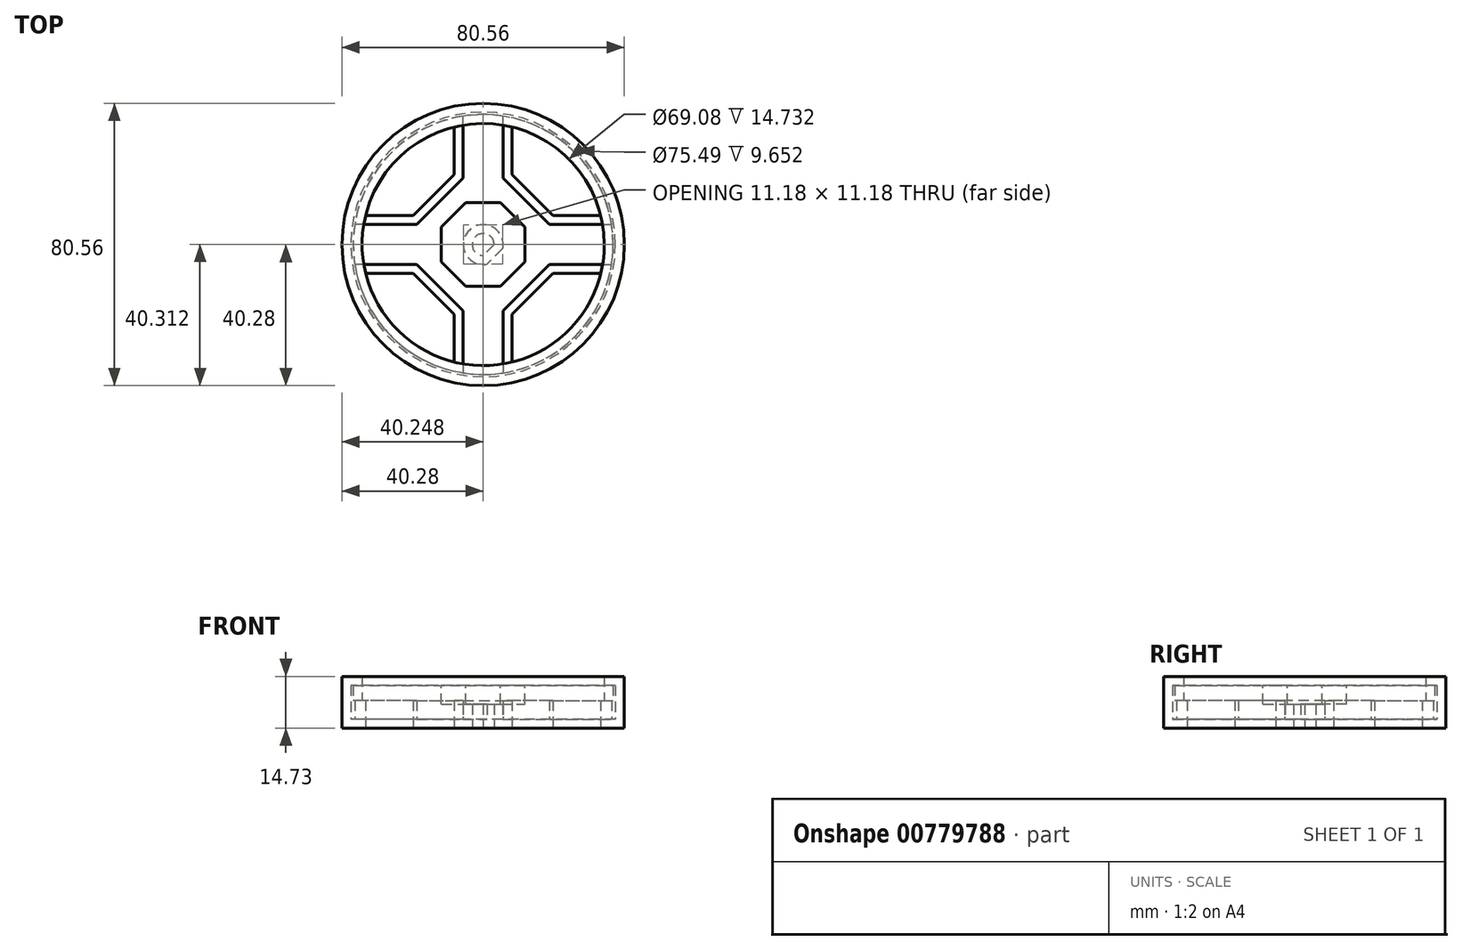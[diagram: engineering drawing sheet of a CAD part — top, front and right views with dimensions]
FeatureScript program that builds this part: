
annotation { "Feature Type Name" : "Feature", "Feature Type Description" : "" }
export const myFeature = defineFeature(function(context is Context, id is Id, definition is map)
    precondition{}
    {
        {
            var Q0;
            Q0=qCreatedBy(makeId("Top.planeOp"),FACE);
            var sketch = newSketch(context, id + "F0", { "sketchPlane" : qUnion([Q0])});
            skCircle(sketch, "E0", {"center": v(0, 0) * mm, "radius": 43.73 * mm});
            skCircle(sketch, "E1", {"center": v(0, 0) * mm, "radius": 34.6 * mm});
            skCircle(sketch, "E2.cCircle", {"center": v(0, 0) * mm, "radius": 19.97 * mm, "construction": true});
            skLineSegment(sketch, "E2.0", {"start": v(-8.27, 19.97) * mm, "end": v(8.27, 19.97) * mm});
            skLineSegment(sketch, "E2.1", {"start": v(8.27, 19.97) * mm, "end": v(19.97, 8.27) * mm});
            skLineSegment(sketch, "E2.2", {"start": v(19.97, 8.27) * mm, "end": v(19.97, -8.27) * mm});
            skLineSegment(sketch, "E2.3", {"start": v(19.97, -8.27) * mm, "end": v(8.27, -19.97) * mm});
            skLineSegment(sketch, "E2.4", {"start": v(8.27, -19.97) * mm, "end": v(-8.27, -19.97) * mm});
            skLineSegment(sketch, "E2.5", {"start": v(-8.27, -19.97) * mm, "end": v(-19.97, -8.27) * mm});
            skLineSegment(sketch, "E2.6", {"start": v(-19.97, -8.27) * mm, "end": v(-19.97, 8.27) * mm});
            skLineSegment(sketch, "E2.7", {"start": v(-19.97, 8.27) * mm, "end": v(-8.27, 19.97) * mm});
            skPoint(sketch, "E2.0.midPoint", {"position": v(0, 19.97) * mm});
            skLineSegment(sketch, "E3", {"start": v(8.27, -19.97) * mm, "end": v(8.27, -33.59) * mm});
            skLineSegment(sketch, "E4", {"start": v(8.27, -33.59) * mm, "end": v(8.27, -19.97) * mm});
            skLineSegment(sketch, "E5", {"start": v(-8.27, -19.97) * mm, "end": v(-8.27, -33.59) * mm});
            skLineSegment(sketch, "E6", {"start": v(-8.27, -33.59) * mm, "end": v(-8.27, -19.97) * mm});
            skLineSegment(sketch, "E7", {"start": v(-19.97, -8.27) * mm, "end": v(-33.59, -8.27) * mm});
            skLineSegment(sketch, "E8", {"start": v(-33.59, -8.27) * mm, "end": v(-19.97, -8.27) * mm});
            skLineSegment(sketch, "E9", {"start": v(-19.97, 8.27) * mm, "end": v(-33.59, 8.27) * mm});
            skLineSegment(sketch, "E10", {"start": v(-33.59, 8.27) * mm, "end": v(-19.97, 8.27) * mm});
            skLineSegment(sketch, "E11", {"start": v(-8.27, 19.97) * mm, "end": v(-8.27, 33.59) * mm});
            skLineSegment(sketch, "E12", {"start": v(-8.27, 33.59) * mm, "end": v(-8.27, 19.97) * mm});
            skLineSegment(sketch, "E13", {"start": v(8.27, 19.97) * mm, "end": v(8.27, 33.59) * mm});
            skLineSegment(sketch, "E14", {"start": v(8.27, 33.59) * mm, "end": v(8.27, 19.97) * mm});
            skLineSegment(sketch, "E15", {"start": v(19.97, 8.27) * mm, "end": v(33.59, 8.27) * mm});
            skLineSegment(sketch, "E16", {"start": v(33.59, 8.27) * mm, "end": v(19.97, 8.27) * mm});
            skLineSegment(sketch, "E17", {"start": v(19.97, -8.27) * mm, "end": v(33.59, -8.27) * mm});
            skLineSegment(sketch, "E18", {"start": v(33.59, -8.27) * mm, "end": v(19.97, -8.27) * mm});
            skSolve(sketch);
        }
        {
            var Q0;
            Q0=makeQuery(id+"F0.imprint","IMPRINT",FACE,{"disambiguationData":[TD([[makeQuery(id+"F0.imprint","IMPRINT",EDGE,{"derivedFrom":sQuery(id+"F0.wireOp",EDGE,"E2.0")}),-1.0]])]});
            var Q1;
            Q1=makeQuery(id+"F0.imprint","IMPRINT",FACE,{"disambiguationData":[TD([[makeQuery(id+"F0.imprint","IMPRINT",EDGE,{"derivedFrom":sQuery(id+"F0.wireOp",EDGE,"E2.6")}),1.0]])]});
            var Q2;
            Q2=makeQuery(id+"F0.imprint","IMPRINT",FACE,{"disambiguationData":[TD([[makeQuery(id+"F0.imprint","IMPRINT",EDGE,{"derivedFrom":sQuery(id+"F0.wireOp",EDGE,"E2.0")}),1.0]])]});
            var Q3;
            Q3=makeQuery(id+"F0.imprint","IMPRINT",FACE,{"disambiguationData":[TD([[makeQuery(id+"F0.imprint","IMPRINT",EDGE,{"derivedFrom":sQuery(id+"F0.wireOp",EDGE,"E2.4")}),1.0]])]});
            var Q4;
            Q4=makeQuery(id+"F0.imprint","IMPRINT",FACE,{"disambiguationData":[TD([[makeQuery(id+"F0.imprint","IMPRINT",EDGE,{"derivedFrom":sQuery(id+"F0.wireOp",EDGE,"E2.2")}),1.0]])]});
            extrude(context, id + "F1", {"entities" : qUnion([Q0, Q1, Q2, Q3, Q4]), "depth" : 7.87 * mm, "offsetDistance" : 25.4 * mm});
        }
        {
            var Q0;
            Q0=qCreatedBy(makeId("Top.planeOp"),FACE);
            var sketch = newSketch(context, id + "F2", { "sketchPlane" : qUnion([Q0])});
            skCircle(sketch, "E19", {"center": v(0, 0) * mm, "radius": 34.54 * mm});
            skCircle(sketch, "E20", {"center": v(0, 0) * mm, "radius": 40.28 * mm});
            skSolve(sketch);
        }
        {
            var Q0;
            Q0 = qSketchRegion(id + "F2", true);
            extrude(context, id + "F3", {"entities" : qUnion([Q0]), "operationType" : NewBodyOperationType.ADD, "depth" : 14.73 * mm, "offsetDistance" : 25.4 * mm});
        }
        {
            var Q0;
            Q0=makeQuery(id+"F3.boolean.opBoolean","MERGE",FACE,{"derivedFrom":[makeQuery(id+"F1.opExtrude","CAP_FACE",FACE,{"disambiguationData":[OSD([sQuery(id+"F0.wireOp",EDGE,"E1"),sQuery(id+"F0.wireOp",EDGE,"E2.1"),sQuery(id+"F0.wireOp",EDGE,"E2.3"),sQuery(id+"F0.wireOp",EDGE,"E2.5"),sQuery(id+"F0.wireOp",EDGE,"E2.7"),sQuery(id+"F0.wireOp",EDGE,"E4"),sQuery(id+"F0.wireOp",EDGE,"E6"),sQuery(id+"F0.wireOp",EDGE,"E8"),sQuery(id+"F0.wireOp",EDGE,"E10"),sQuery(id+"F0.wireOp",EDGE,"E12"),sQuery(id+"F0.wireOp",EDGE,"E14"),sQuery(id+"F0.wireOp",EDGE,"E16"),sQuery(id+"F0.wireOp",EDGE,"E18")])],"isStart":true}),makeQuery(id+"F3.opExtrude","CAP_FACE",FACE,{"disambiguationData":[OSD([sQuery(id+"F2.wireOp",EDGE,"E19"),sQuery(id+"F2.wireOp",EDGE,"E20")])],"isStart":true})]});
            var sketch = newSketch(context, id + "F4", { "sketchPlane" : qUnion([Q0])});
            skArc(sketch, "E21", {"start": v(0, 3.14) * mm, "mid": v(-2.22, -2.22) * mm, "end": v(3.14, 0) * mm});
            skLineSegment(sketch, "E22", {"start": v(3.14, 0) * mm, "end": v(0, 3.14) * mm});
            skSolve(sketch);
        }
        {
            var Q0;
            Q0 = qSketchRegion(id + "F4", true);
            extrude(context, id + "F5", {"entities" : qUnion([Q0]), "operationType" : NewBodyOperationType.REMOVE, "oppositeDirection" : true, "depth" : 25.4 * mm, "offsetDistance" : 25.4 * mm});
        }
        {
            var Q0;
            Q0=makeQuery(id+"F1.opExtrude","CAP_FACE",FACE,{"disambiguationData":[OSD([sQuery(id+"F0.wireOp",EDGE,"E1"),sQuery(id+"F0.wireOp",EDGE,"E2.1"),sQuery(id+"F0.wireOp",EDGE,"E2.3"),sQuery(id+"F0.wireOp",EDGE,"E2.5"),sQuery(id+"F0.wireOp",EDGE,"E2.7"),sQuery(id+"F0.wireOp",EDGE,"E4"),sQuery(id+"F0.wireOp",EDGE,"E6"),sQuery(id+"F0.wireOp",EDGE,"E8"),sQuery(id+"F0.wireOp",EDGE,"E10"),sQuery(id+"F0.wireOp",EDGE,"E12"),sQuery(id+"F0.wireOp",EDGE,"E14"),sQuery(id+"F0.wireOp",EDGE,"E16"),sQuery(id+"F0.wireOp",EDGE,"E18")])],"isStart":false});
            shell(context, id + "F6", {"entities" : qUnion([Q0]), "thickness" : 2.54 * mm});
        }
        {
            var Q0;
            Q0=makeQuery(id+"F6.opShell","OFFSET_FACE",FACE,{"disambiguationData":[OSD([sQuery(id+"F0.wireOp",EDGE,"E1"),sQuery(id+"F0.wireOp",EDGE,"E2.1"),sQuery(id+"F0.wireOp",EDGE,"E2.3"),sQuery(id+"F0.wireOp",EDGE,"E2.5"),sQuery(id+"F0.wireOp",EDGE,"E2.7"),sQuery(id+"F0.wireOp",EDGE,"E4"),sQuery(id+"F0.wireOp",EDGE,"E6"),sQuery(id+"F0.wireOp",EDGE,"E8"),sQuery(id+"F0.wireOp",EDGE,"E10"),sQuery(id+"F0.wireOp",EDGE,"E12"),sQuery(id+"F0.wireOp",EDGE,"E14"),sQuery(id+"F0.wireOp",EDGE,"E16"),sQuery(id+"F0.wireOp",EDGE,"E18"),sQuery(id+"F2.wireOp",EDGE,"E19"),sQuery(id+"F2.wireOp",EDGE,"E20")])]});
            var sketch = newSketch(context, id + "F7", { "sketchPlane" : qUnion([Q0])});
            skCircle(sketch, "E23.cCircle", {"center": v(0, 0) * mm, "radius": 11.92 * mm, "construction": true});
            skLineSegment(sketch, "E23.0", {"start": v(11.92, 4.94) * mm, "end": v(11.92, -4.94) * mm});
            skLineSegment(sketch, "E23.1", {"start": v(11.92, -4.94) * mm, "end": v(4.94, -11.92) * mm});
            skLineSegment(sketch, "E23.2", {"start": v(4.94, -11.92) * mm, "end": v(-4.94, -11.92) * mm});
            skLineSegment(sketch, "E23.3", {"start": v(-4.94, -11.92) * mm, "end": v(-11.92, -4.94) * mm});
            skLineSegment(sketch, "E23.4", {"start": v(-11.92, -4.94) * mm, "end": v(-11.92, 4.94) * mm});
            skLineSegment(sketch, "E23.5", {"start": v(-11.92, 4.94) * mm, "end": v(-4.94, 11.92) * mm});
            skLineSegment(sketch, "E23.6", {"start": v(-4.94, 11.92) * mm, "end": v(4.94, 11.92) * mm});
            skLineSegment(sketch, "E23.7", {"start": v(4.94, 11.92) * mm, "end": v(11.92, 4.94) * mm});
            skPoint(sketch, "E23.0.midPoint", {"position": v(11.92, 0) * mm});
            skSolve(sketch);
        }
        {
            var Q0;
            Q0=makeQuery(id+"F7.imprint","IMPRINT",FACE,{"disambiguationData":[TD([[makeQuery(id+"F7.imprint","IMPRINT",EDGE,{"derivedFrom":sQuery(id+"F7.wireOp",EDGE,"E23.0")}),-1.0]])]});
            extrude(context, id + "F8", {"entities" : qUnion([Q0]), "operationType" : NewBodyOperationType.ADD, "depth" : 5.36 * mm, "offsetDistance" : 25.4 * mm});
        }
    });
